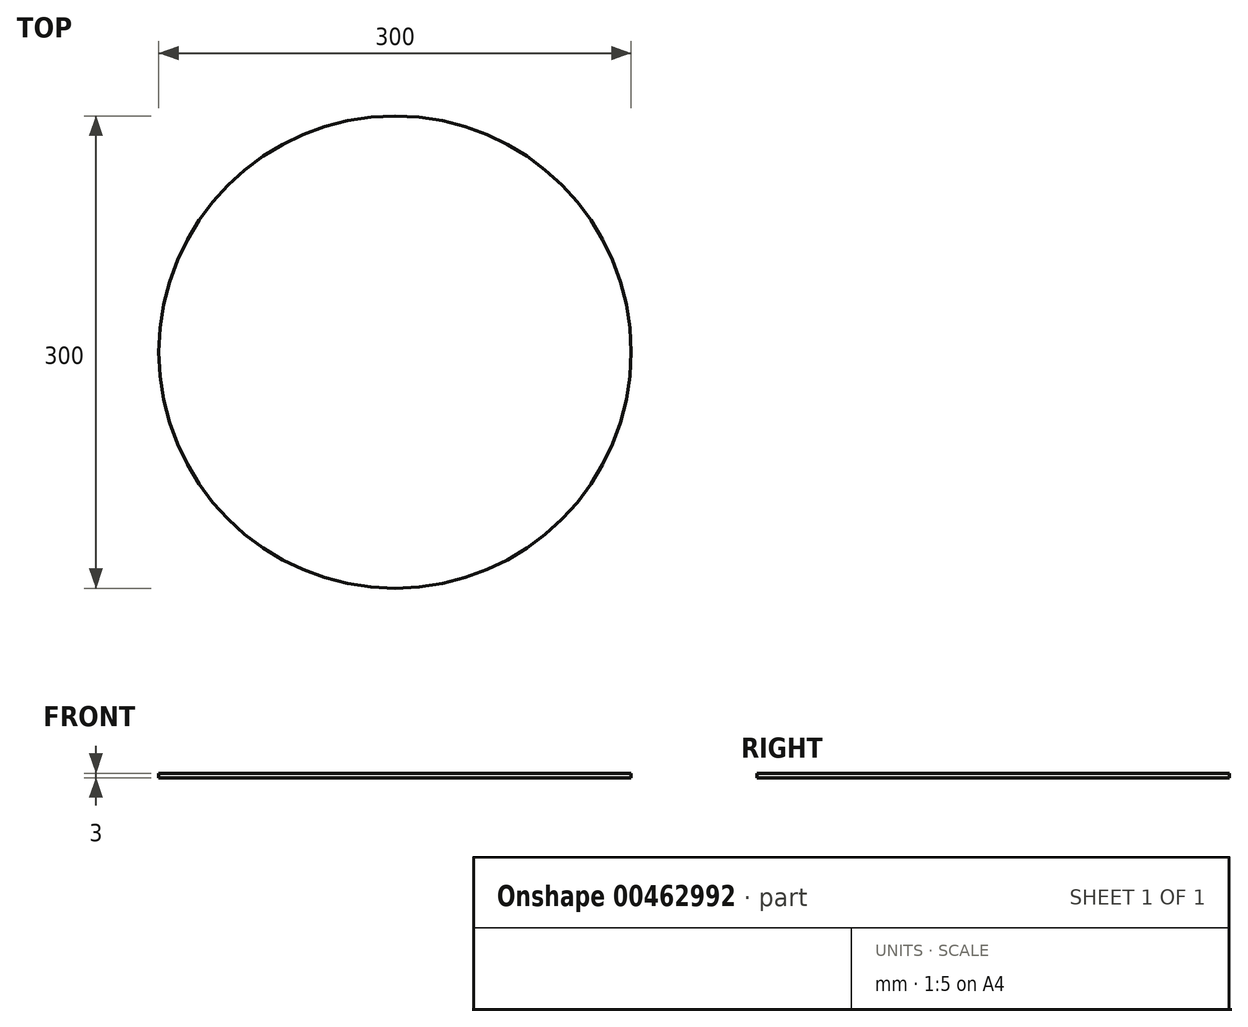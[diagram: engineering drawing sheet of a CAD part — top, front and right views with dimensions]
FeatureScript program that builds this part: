
annotation { "Feature Type Name" : "Feature", "Feature Type Description" : "" }
export const myFeature = defineFeature(function(context is Context, id is Id, definition is map)
    precondition{}
    {
        {
            var Q0;
            Q0=qCreatedBy(makeId("Top.planeOp"),FACE);
            var sketch = newSketch(context, id + "F0", { "sketchPlane" : qUnion([Q0])});
            skCircle(sketch, "E0", {"center": v(0, 0) * mm, "radius": 150 * mm});
            skSolve(sketch);
        }
        {
            var Q0;
            Q0 = qSketchRegion(id + "F0", true);
            extrude(context, id + "F1", {"entities" : qUnion([Q0]), "depth" : 3 * mm, "offsetDistance" : 25 * mm});
        }
    });
